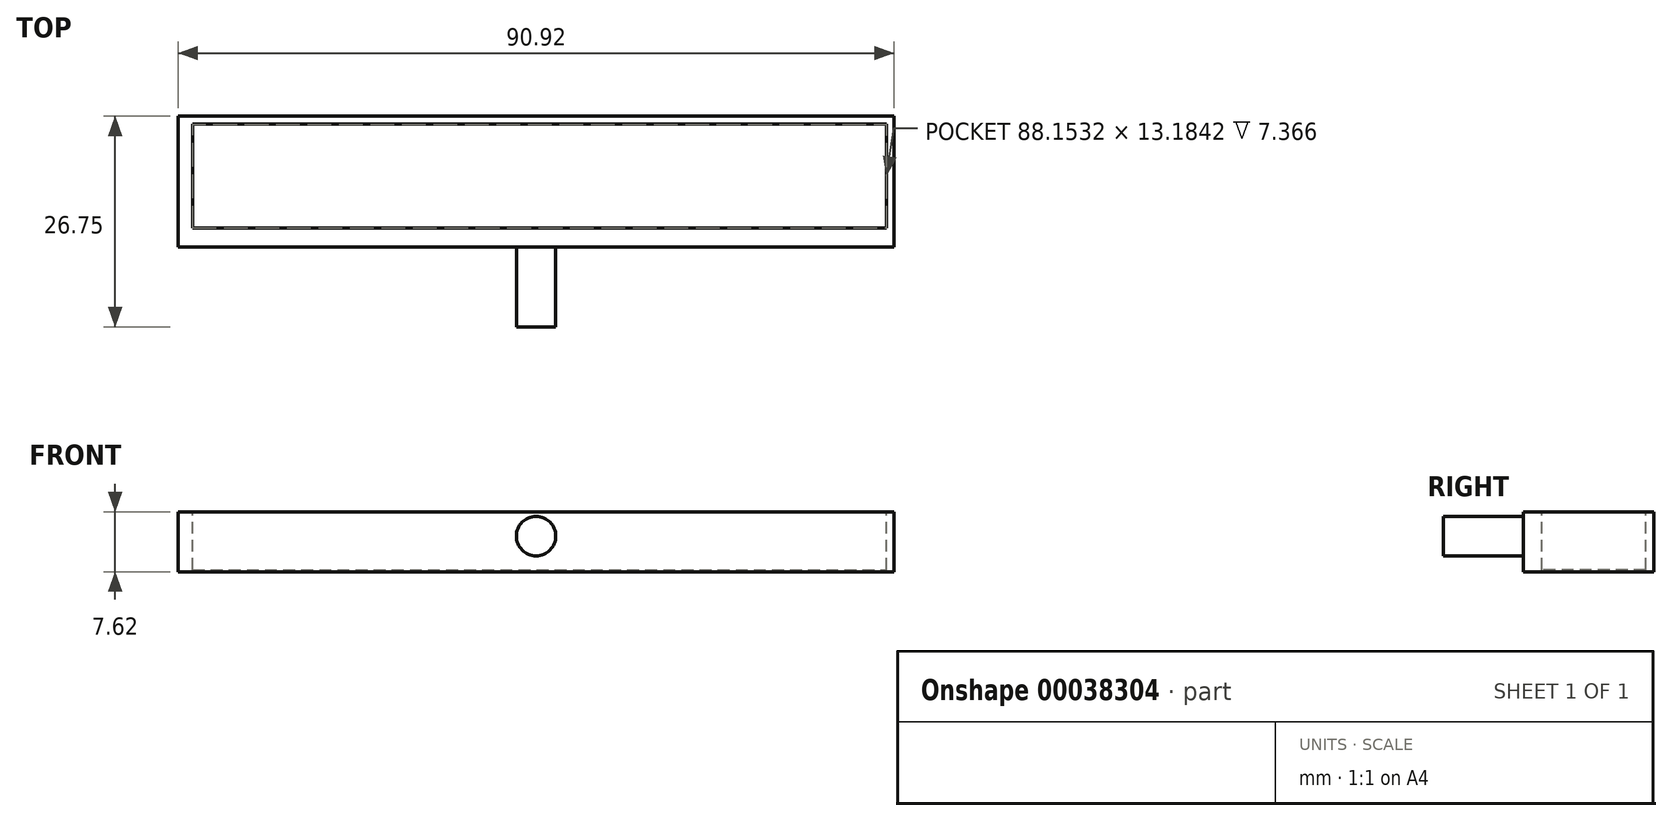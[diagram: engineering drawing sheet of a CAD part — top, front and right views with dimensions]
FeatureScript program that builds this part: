
annotation { "Feature Type Name" : "Feature", "Feature Type Description" : "" }
export const myFeature = defineFeature(function(context is Context, id is Id, definition is map)
    precondition{}
    {
        {
            var Q0;
            Q0=qCreatedBy(makeId("Top.planeOp"),FACE);
            var sketch = newSketch(context, id + "F0", { "sketchPlane" : qUnion([Q0])});
            skLineSegment(sketch, "E0.bottom", {"start": v(-59.74, -43.82) * mm, "end": v(31.18, -43.82) * mm});
            skLineSegment(sketch, "E0.top", {"start": v(-59.74, -60.41) * mm, "end": v(31.18, -60.41) * mm});
            skLineSegment(sketch, "E0.left", {"start": v(-59.74, -43.82) * mm, "end": v(-59.74, -60.41) * mm});
            skLineSegment(sketch, "E0.right", {"start": v(31.18, -43.82) * mm, "end": v(31.18, -60.41) * mm});
            skSolve(sketch);
        }
        {
            var Q0;
            Q0 = qSketchRegion(id + "F0", true);
            extrude(context, id + "F1", {"entities" : qUnion([Q0]), "depth" : 7.62 * mm});
        }
        {
            var Q0;
            Q0=makeQuery(id+"F1.opExtrude","CAP_FACE",FACE,{"disambiguationData":[OSD([sQuery(id+"F0.wireOp",EDGE,"E0.bottom"),sQuery(id+"F0.wireOp",EDGE,"E0.top"),sQuery(id+"F0.wireOp",EDGE,"E0.left"),sQuery(id+"F0.wireOp",EDGE,"E0.right")])],"isStart":false});
            var sketch = newSketch(context, id + "F2", { "sketchPlane" : qUnion([Q0])});
            skLineSegment(sketch, "E1.bottom", {"start": v(-57.9, -44.85) * mm, "end": v(30.25, -44.85) * mm});
            skLineSegment(sketch, "E1.top", {"start": v(-57.9, -58.04) * mm, "end": v(30.25, -58.04) * mm});
            skLineSegment(sketch, "E1.left", {"start": v(-57.9, -44.85) * mm, "end": v(-57.9, -58.04) * mm});
            skLineSegment(sketch, "E1.right", {"start": v(30.25, -44.85) * mm, "end": v(30.25, -58.04) * mm});
            skSolve(sketch);
        }
        {
            var Q0;
            Q0=makeQuery(id+"F1.opExtrude","SWEPT_FACE",FACE,{"disambiguationData":[OSD([sQuery(id+"F0.wireOp",EDGE,"E0.top")])]});
            var sketch = newSketch(context, id + "F3", { "sketchPlane" : qUnion([Q0])});
            skCircle(sketch, "E2", {"center": v(-14.28, 4.52) * mm, "radius": 2.5 * mm});
            skPoint(sketch, "E2.centerSnap0", {"position": v(-14.28, 0) * mm});
            skSolve(sketch);
        }
        {
            var Q0;
            Q0 = qSketchRegion(id + "F3", true);
            extrude(context, id + "F4", {"entities" : qUnion([Q0]), "operationType" : NewBodyOperationType.ADD, "depth" : 10.16 * mm});
        }
        {
            var Q0;
            Q0=makeQuery(id+"F2.imprint","IMPRINT",FACE,{"disambiguationData":[TD([[makeQuery(id+"F2.imprint","IMPRINT",EDGE,{"derivedFrom":sQuery(id+"F2.wireOp",EDGE,"E1.bottom")}),-1.0]])]});
            extrude(context, id + "F5", {"entities" : qUnion([Q0]), "operationType" : NewBodyOperationType.REMOVE, "oppositeDirection" : true, "depth" : 7.37 * mm});
        }
    });
